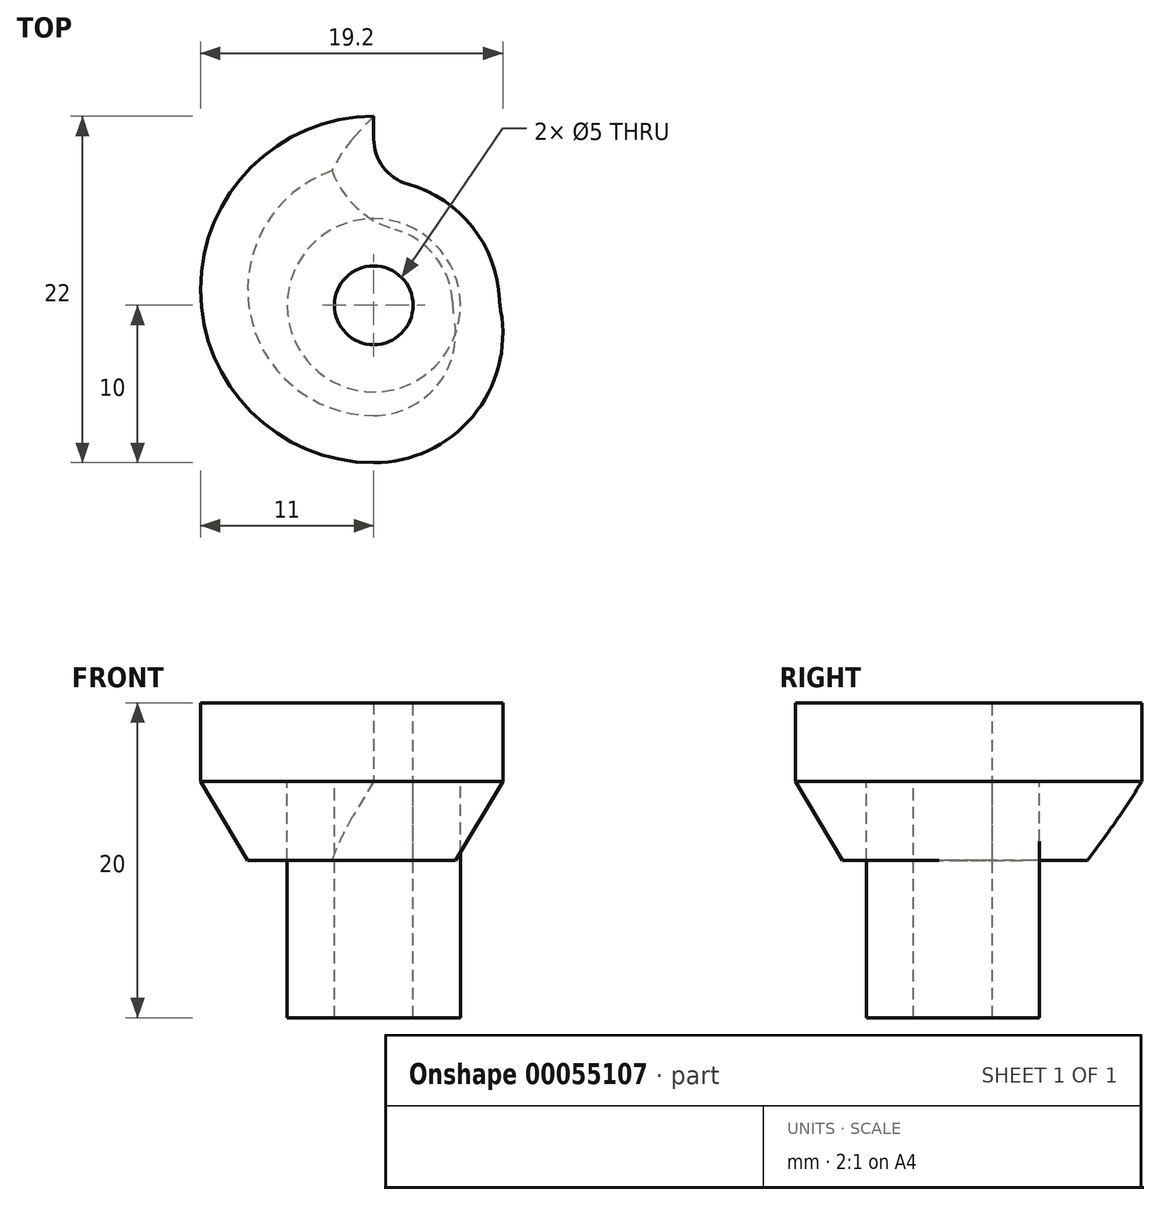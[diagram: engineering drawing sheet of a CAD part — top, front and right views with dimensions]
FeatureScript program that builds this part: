
annotation { "Feature Type Name" : "Feature", "Feature Type Description" : "" }
export const myFeature = defineFeature(function(context is Context, id is Id, definition is map)
    precondition{}
    {
        {
            var Q0;
            Q0=qCreatedBy(makeId("Top.planeOp"),FACE);
            var sketch = newSketch(context, id + "F0", { "sketchPlane" : qUnion([Q0])});
            skArc(sketch, "E0", {"start": v(-10.95, 0) * mm, "mid": v(-7.42, -7.12) * mm, "end": v(0, -10) * mm});
            skLineSegment(sketch, "E1", {"start": v(0, 11.88) * mm, "end": v(0, -10.55) * mm, "construction": true});
            skLineSegment(sketch, "E2", {"start": v(-10.37, 0) * mm, "end": v(12.86, 0) * mm, "construction": true});
            skArc(sketch, "E3.trimOffspring", {"start": v(0, -10) * mm, "mid": v(6.4, -6.92) * mm, "end": v(8, 0) * mm});
            skPoint(sketch, "E4.center.orphan", {"position": v(0, -1) * mm});
            skArc(sketch, "E5", {"start": v(0, 12) * mm, "mid": v(-11, 1) * mm, "end": v(0, -10) * mm});
            skLineSegment(sketch, "E6", {"start": v(0, 12) * mm, "end": v(0, 8) * mm});
            skArc(sketch, "E7", {"start": v(8, 0) * mm, "mid": v(5.66, 5.66) * mm, "end": v(0, 8) * mm});
            skSolve(sketch);
        }
        {
            var Q0;
            {var subQ0=sQuery(id+"F0.wireOp",EDGE,"E3.trimOffspring");Q0=makeQuery(id+"F0.imprint","IMPRINT",FACE,{"disambiguationData":[TD([[makeQuery(id+"F0.imprint","IMPRINT",EDGE,{"derivedFrom":subQ0}),1.0]])]});}
            extrude(context, id + "F1", {"entities" : qUnion([Q0]), "depth" : 10 * mm});
        }
        {
            var Q0;
            Q0=makeQuery(id+"F1.opExtrude","SWEPT_EDGE",EDGE,{"disambiguationData":[OSD([sQuery(id+"F0.wireOp",EDGE,"E3.trimOffspring"),sQuery(id+"F0.wireOp",EDGE,"E7")])]});
            fillet(context, id + "F2", {"entities" : qUnion([Q0]), "radius" : 5 * mm, "tangentPropagation" : true, "allowEdgeOverflow" : false});
        }
        {
            var Q0;
            Q0=makeQuery(id+"F1.opExtrude","SWEPT_EDGE",EDGE,{"disambiguationData":[OSD([sQuery(id+"F0.wireOp",EDGE,"E6"),sQuery(id+"F0.wireOp",EDGE,"E7")])]});
            fillet(context, id + "F3", {"entities" : qUnion([Q0]), "radius" : 3 * mm, "tangentPropagation" : true, "allowEdgeOverflow" : false});
        }
        {
            var Q0;
            Q0=makeQuery(id+"F1.opExtrude","CAP_EDGE",EDGE,{"disambiguationData":[OSD([sQuery(id+"F0.wireOp",EDGE,"E3.trimOffspring")])],"isStart":true});
            var Q1;
            Q1=makeQuery(id+"F1.opExtrude","CAP_EDGE",EDGE,{"disambiguationData":[OSD([sQuery(id+"F0.wireOp",EDGE,"E5")])],"isStart":true});
            var Q2;
            {var subQ0=sQuery(id+"F0.wireOp",EDGE,"E7");var subQ1=sQuery(id+"F0.wireOp",EDGE,"E3.trimOffspring");Q2=makeQuery(id+"F2.opFillet","BLEND_EDGE",EDGE,{"blendedFrom":[makeQuery(id+"F1.opExtrude","SWEPT_EDGE",EDGE,{"disambiguationData":[OSD([subQ1,subQ0])]}),makeQuery(id+"F1.opExtrude","CAP_FACE",FACE,{"disambiguationData":[OSD([subQ1,sQuery(id+"F0.wireOp",EDGE,"E5"),sQuery(id+"F0.wireOp",EDGE,"E6"),subQ0])],"isStart":true})],"blendedInto":[makeQuery(id+"F1.opExtrude","CAP_FACE",FACE,{"disambiguationData":[OSD([subQ1,sQuery(id+"F0.wireOp",EDGE,"E5"),sQuery(id+"F0.wireOp",EDGE,"E6"),subQ0])],"isStart":true})]});}
            var Q3;
            Q3=makeQuery(id+"F1.opExtrude","CAP_EDGE",EDGE,{"disambiguationData":[OSD([sQuery(id+"F0.wireOp",EDGE,"E7")])],"isStart":true});
            var Q4;
            {var subQ0=sQuery(id+"F0.wireOp",EDGE,"E7");var subQ1=sQuery(id+"F0.wireOp",EDGE,"E6");Q4=makeQuery(id+"F3.opFillet","BLEND_EDGE",EDGE,{"blendedFrom":[makeQuery(id+"F1.opExtrude","SWEPT_EDGE",EDGE,{"disambiguationData":[OSD([subQ1,subQ0])]}),makeQuery(id+"F1.opExtrude","CAP_FACE",FACE,{"disambiguationData":[OSD([sQuery(id+"F0.wireOp",EDGE,"E3.trimOffspring"),sQuery(id+"F0.wireOp",EDGE,"E5"),subQ1,subQ0])],"isStart":true})],"blendedInto":[makeQuery(id+"F1.opExtrude","CAP_FACE",FACE,{"disambiguationData":[OSD([sQuery(id+"F0.wireOp",EDGE,"E3.trimOffspring"),sQuery(id+"F0.wireOp",EDGE,"E5"),subQ1,subQ0])],"isStart":true})]});}
            chamfer(context, id + "F4", {"entities" : qUnion([Q0, Q1, Q2, Q3, Q4]), "chamferType" : ChamferType.TWO_OFFSETS, "width1" : 5 * mm, "oppositeDirection" : false, "width2" : 3 * mm, "tangentPropagation" : true});
        }
        {
            var Q0;
            {var subQ0=sQuery(id+"F0.wireOp",EDGE,"E3.trimOffspring");Q0=makeQuery(id+"F0.imprint","IMPRINT",FACE,{"disambiguationData":[TD([[makeQuery(id+"F0.imprint","IMPRINT",EDGE,{"derivedFrom":subQ0}),1.0]])]});}
            var sketch = newSketch(context, id + "F5", { "sketchPlane" : qUnion([Q0])});
            skCircle(sketch, "E8", {"center": v(0, 0) * mm, "radius": 5.5 * mm});
            skSolve(sketch);
        }
        {
            var Q0;
            Q0=makeQuery(id+"F5.imprint","IMPRINT",FACE,{"disambiguationData":[TD([[makeQuery(id+"F5.imprint","IMPRINT",EDGE,{"derivedFrom":sQuery(id+"F5.wireOp",EDGE,"E8")}),1.0]])]});
            extrude(context, id + "F6", {"entities" : qUnion([Q0]), "oppositeDirection" : true, "depth" : 10 * mm, "hasSecondDirection" : true, "secondDirectionOppositeDirection" : false, "secondDirectionDepth" : 5 * mm});
        }
        {
            var Q0;
            Q0=makeQuery(id+"F1.opExtrude","CAP_FACE",FACE,{"disambiguationData":[OSD([sQuery(id+"F0.wireOp",EDGE,"E3.trimOffspring"),sQuery(id+"F0.wireOp",EDGE,"E5"),sQuery(id+"F0.wireOp",EDGE,"E6"),sQuery(id+"F0.wireOp",EDGE,"E7")])],"isStart":false});
            var sketch = newSketch(context, id + "F7", { "sketchPlane" : qUnion([Q0])});
            skCircle(sketch, "E9", {"center": v(0, 0) * mm, "radius": 2.5 * mm});
            skSolve(sketch);
        }
        {
            var Q0;
            Q0 = qSketchRegion(id + "F7", true);
            extrude(context, id + "F8", {"entities" : qUnion([Q0]), "operationType" : NewBodyOperationType.REMOVE, "endBound" : BoundingType.THROUGH_ALL, "oppositeDirection" : true, "depth" : 25 * mm});
        }
    });
